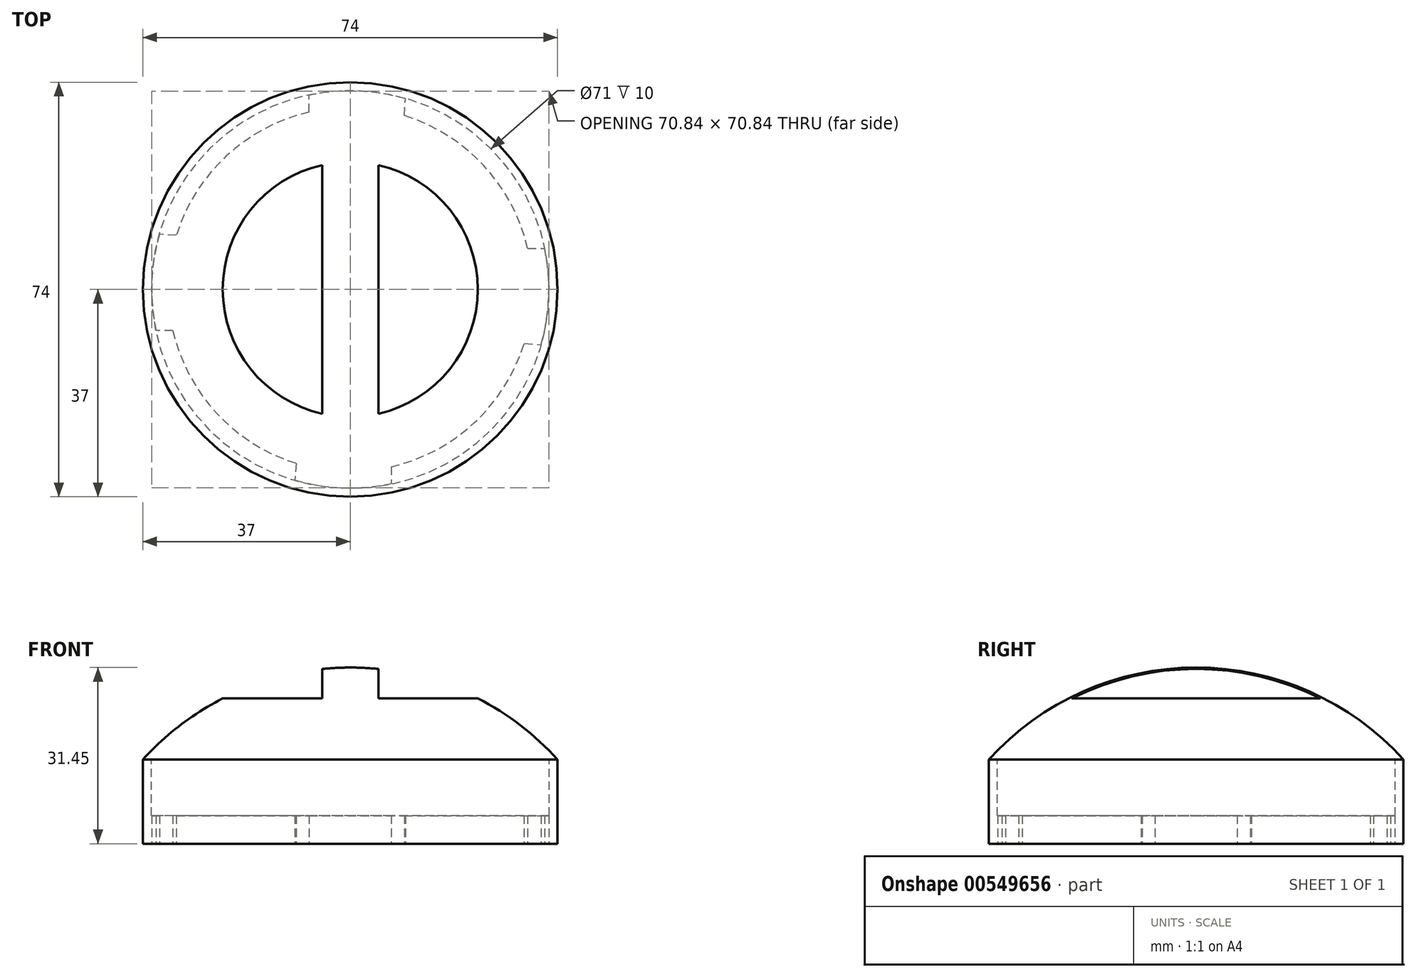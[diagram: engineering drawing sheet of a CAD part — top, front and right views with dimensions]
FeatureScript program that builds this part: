
annotation { "Feature Type Name" : "Feature", "Feature Type Description" : "" }
export const myFeature = defineFeature(function(context is Context, id is Id, definition is map)
    precondition{}
    {
        {
            var Q0;
            Q0=qCreatedBy(makeId("Front.planeOp"),FACE);
            var sketch = newSketch(context, id + "F0", { "sketchPlane" : qUnion([Q0])});
            skCircle(sketch, "E0", {"center": v(0, -43.55) * mm, "radius": 60 * mm, "construction": true});
            skLineSegment(sketch, "E1", {"start": v(0, 0) * mm, "end": v(0, 16.45) * mm, "construction": true});
            skSolve(sketch);
        }
        {
            var Q0;
            Q0=qCreatedBy(makeId("Front.planeOp"),FACE);
            var sketch = newSketch(context, id + "F1", { "sketchPlane" : qUnion([Q0])});
            skLineSegment(sketch, "E2", {"start": v(0, 0) * mm, "end": v(0, 16.45) * mm});
            skLineSegment(sketch, "E3", {"start": v(0, 0) * mm, "end": v(-37, 0) * mm});
            skArc(sketch, "E4", {"start": v(0, 16.45) * mm, "mid": v(-20.25, 12.15) * mm, "end": v(-37, 0) * mm});
            skSolve(sketch);
        }
        {
            var Q0;
            Q0 = qSketchRegion(id + "F1", true);
            var Q1;
            Q1=sQuery(id+"F1.wireOp",EDGE,"E2");
            revolve(context, id + "F2", {"entities" : qUnion([Q0]), "axis" : qUnion([Q1]), "revolveType" : RevolveType.FULL});
        }
        {
            var Q0;
            Q0=qCreatedBy(makeId("Top.planeOp"),FACE);
            cPlane(context, id + "F3", {"entities" : qUnion([Q0]), "cplaneType" : CPlaneType.OFFSET, "offset" : 16.45 * mm, "width" : 150 * mm, "height" : 150 * mm});
        }
        {
            var Q0;
            Q0=qCreatedBy(id+"F3.planeOp",FACE);
            var sketch = newSketch(context, id + "F4", { "sketchPlane" : qUnion([Q0])});
            skLineSegment(sketch, "E5.bottom", {"start": v(-25, 25) * mm, "end": v(-5, 25) * mm});
            skLineSegment(sketch, "E5.top", {"start": v(-25, -25) * mm, "end": v(-5, -25) * mm});
            skLineSegment(sketch, "E5.left", {"start": v(-25, 25) * mm, "end": v(-25, -25) * mm});
            skLineSegment(sketch, "E5.right", {"start": v(-5, 25) * mm, "end": v(-5, -25) * mm});
            skLineSegment(sketch, "E6.MirrorCS", {"start": v(5, 25) * mm, "end": v(5, -25) * mm});
            skLineSegment(sketch, "E7.MirrorCS", {"start": v(25, 25) * mm, "end": v(5, 25) * mm});
            skLineSegment(sketch, "E8.MirrorCS", {"start": v(25, 25) * mm, "end": v(25, -25) * mm});
            skLineSegment(sketch, "E9.MirrorCS", {"start": v(25, -25) * mm, "end": v(5, -25) * mm});
            skSolve(sketch);
        }
        {
            var Q0;
            Q0=qCreatedBy(makeId("Top.planeOp"),FACE);
            var sketch = newSketch(context, id + "F5", { "sketchPlane" : qUnion([Q0])});
            skCircle(sketch, "E10", {"center": v(0, 0) * mm, "radius": 37 * mm});
            skCircle(sketch, "E11", {"center": v(0, 0) * mm, "radius": 35.5 * mm});
            skSolve(sketch);
        }
        {
            var Q0;
            Q0 = qSketchRegion(id + "F5", true);
            extrude(context, id + "F6", {"entities" : qUnion([Q0]), "operationType" : NewBodyOperationType.ADD, "oppositeDirection" : true, "depth" : 10 * mm, "offsetDistance" : 25 * mm});
        }
        {
            var Q0;
            Q0=makeQuery(id+"F6.opExtrude","CAP_FACE",FACE,{"disambiguationData":[OSD([sQuery(id+"F5.wireOp",EDGE,"E10"),sQuery(id+"F5.wireOp",EDGE,"E11")])],"isStart":false});
            var sketch = newSketch(context, id + "F7", { "sketchPlane" : qUnion([Q0])});
            skCircle(sketch, "E12", {"center": v(0, 0) * mm, "radius": 37 * mm});
            skCircle(sketch, "E13", {"center": v(0, 0) * mm, "radius": 32.5 * mm});
            skSolve(sketch);
        }
        {
            var Q0;
            Q0 = qSketchRegion(id + "F7", true);
            extrude(context, id + "F8", {"entities" : qUnion([Q0]), "operationType" : NewBodyOperationType.ADD, "depth" : 5 * mm, "offsetDistance" : 25 * mm});
        }
        {
            var Q0;
            Q0 = qSketchRegion(id + "F4", true);
            extrude(context, id + "F9", {"entities" : qUnion([Q0]), "operationType" : NewBodyOperationType.REMOVE, "oppositeDirection" : true, "depth" : 5.5 * mm, "offsetDistance" : 25 * mm});
        }
        {
            var Q0;
            Q0=makeQuery(id+"F8.opExtrude","CAP_FACE",FACE,{"disambiguationData":[OSD([sQuery(id+"F7.wireOp",EDGE,"E12"),sQuery(id+"F7.wireOp",EDGE,"E13")])],"isStart":false});
            var sketch = newSketch(context, id + "F10", { "sketchPlane" : qUnion([Q0])});
            skArc(sketch, "E14", {"start": v(-9.65, 31.04) * mm, "mid": v(-1.2, 32.48) * mm, "end": v(7.34, 31.66) * mm});
            skArc(sketch, "E15", {"start": v(-9.86, 34.03) * mm, "mid": v(-1.3, 35.4) * mm, "end": v(7.34, 34.66) * mm});
            skLineSegment(sketch, "E16", {"start": v(-9.65, 31.04) * mm, "end": v(-9.86, 34.03) * mm});
            skLineSegment(sketch, "E17", {"start": v(7.34, 31.66) * mm, "end": v(7.34, 34.66) * mm});
            skLineSegment(sketch, "E18.1.0", {"start": v(-31.04, -9.65) * mm, "end": v(-34.03, -9.86) * mm});
            skLineSegment(sketch, "E18.1.1", {"start": v(-31.66, 7.34) * mm, "end": v(-34.66, 7.34) * mm});
            skArc(sketch, "E18.1.2", {"start": v(-34.03, -9.86) * mm, "mid": v(-35.4, -1.3) * mm, "end": v(-34.66, 7.34) * mm});
            skArc(sketch, "E18.1.3", {"start": v(-31.04, -9.65) * mm, "mid": v(-32.48, -1.2) * mm, "end": v(-31.66, 7.34) * mm});
            skLineSegment(sketch, "E18.2.0", {"start": v(9.65, -31.04) * mm, "end": v(9.86, -34.03) * mm});
            skLineSegment(sketch, "E18.2.1", {"start": v(-7.34, -31.66) * mm, "end": v(-7.34, -34.66) * mm});
            skArc(sketch, "E18.2.2", {"start": v(9.86, -34.03) * mm, "mid": v(1.3, -35.4) * mm, "end": v(-7.34, -34.66) * mm});
            skArc(sketch, "E18.2.3", {"start": v(9.65, -31.04) * mm, "mid": v(1.2, -32.48) * mm, "end": v(-7.34, -31.66) * mm});
            skLineSegment(sketch, "E18.3.0", {"start": v(31.04, 9.65) * mm, "end": v(34.03, 9.86) * mm});
            skLineSegment(sketch, "E18.3.1", {"start": v(31.66, -7.34) * mm, "end": v(34.66, -7.34) * mm});
            skArc(sketch, "E18.3.2", {"start": v(34.03, 9.86) * mm, "mid": v(35.4, 1.3) * mm, "end": v(34.66, -7.34) * mm});
            skArc(sketch, "E18.3.3", {"start": v(31.04, 9.65) * mm, "mid": v(32.48, 1.2) * mm, "end": v(31.66, -7.34) * mm});
            skSolve(sketch);
        }
        {
            var Q0;
            Q0=makeQuery(id+"F10.imprint","IMPRINT",FACE,{"disambiguationData":[TD([[makeQuery(id+"F10.imprint","IMPRINT",EDGE,{"derivedFrom":sQuery(id+"F10.wireOp",EDGE,"E18.1.0")}),-1.0]])]});
            var Q1;
            Q1=makeQuery(id+"F10.imprint","IMPRINT",FACE,{"disambiguationData":[TD([[makeQuery(id+"F10.imprint","IMPRINT",EDGE,{"derivedFrom":sQuery(id+"F10.wireOp",EDGE,"E18.2.0")}),-1.0]])]});
            var Q2;
            Q2=makeQuery(id+"F10.imprint","IMPRINT",FACE,{"disambiguationData":[TD([[makeQuery(id+"F10.imprint","IMPRINT",EDGE,{"derivedFrom":sQuery(id+"F10.wireOp",EDGE,"E18.3.0")}),-1.0]])]});
            var Q3;
            Q3=makeQuery(id+"F10.imprint","IMPRINT",FACE,{"disambiguationData":[TD([[makeQuery(id+"F10.imprint","IMPRINT",EDGE,{"derivedFrom":sQuery(id+"F10.wireOp",EDGE,"E14")}),-1.0]])]});
            extrude(context, id + "F11", {"entities" : qUnion([Q0, Q1, Q2, Q3]), "operationType" : NewBodyOperationType.REMOVE, "oppositeDirection" : true, "depth" : 10 * mm, "offsetDistance" : 25 * mm});
        }
    });
